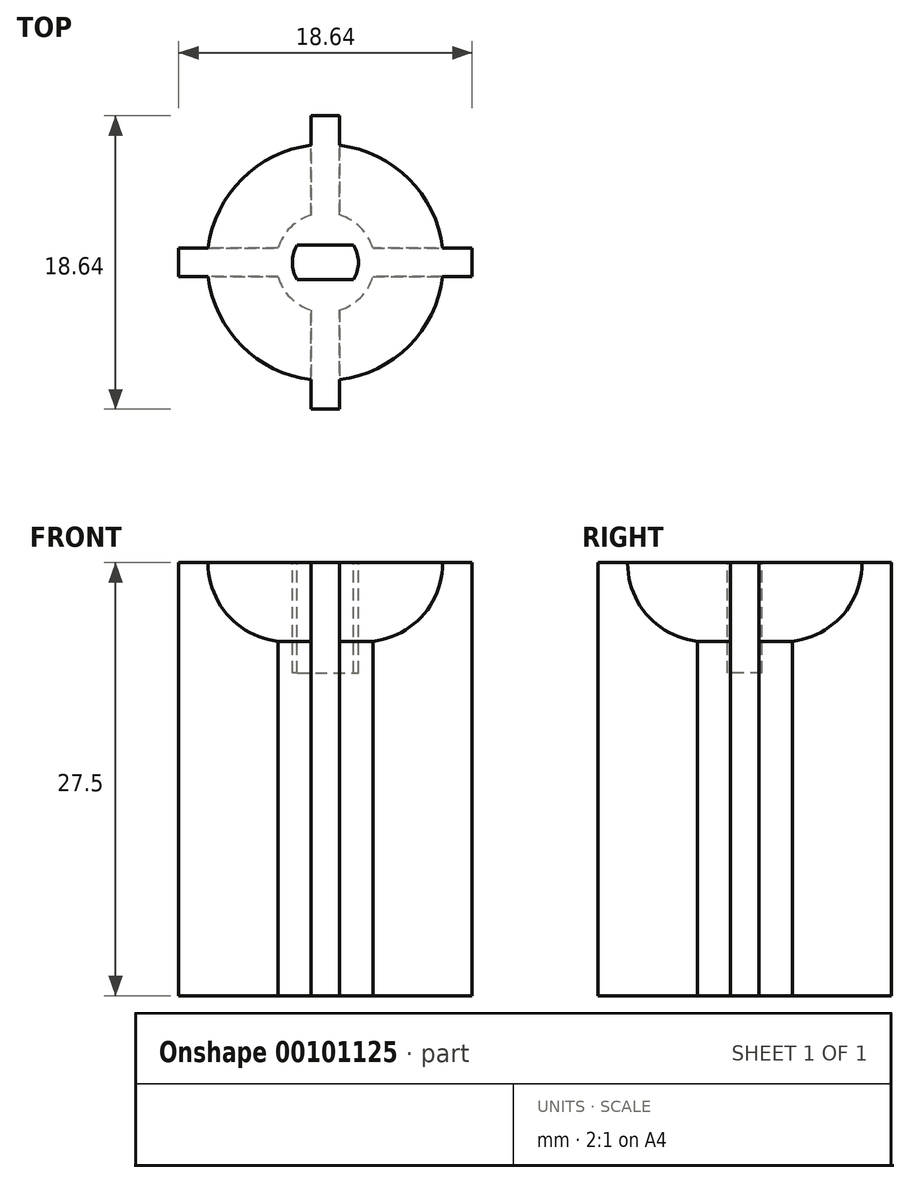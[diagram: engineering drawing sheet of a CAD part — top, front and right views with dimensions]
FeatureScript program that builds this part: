
annotation { "Feature Type Name" : "Feature", "Feature Type Description" : "" }
export const myFeature = defineFeature(function(context is Context, id is Id, definition is map)
    precondition{}
    {
        {
            var Q0;
            Q0=qCreatedBy(makeId("Top.planeOp"),FACE);
            var sketch = newSketch(context, id + "F0", { "sketchPlane" : qUnion([Q0])});
            skCircle(sketch, "E0", {"center": v(0, 0) * mm, "radius": 3.15 * mm});
            skLineSegment(sketch, "E1", {"start": v(-3.02, 0.9) * mm, "end": v(-9.32, 0.9) * mm});
            skLineSegment(sketch, "E2", {"start": v(-9.32, 0.9) * mm, "end": v(-9.32, -0.9) * mm});
            skLineSegment(sketch, "E3", {"start": v(-9.32, -0.9) * mm, "end": v(-3.02, -0.9) * mm});
            skLineSegment(sketch, "E4.1.0", {"start": v(-0.9, -3.02) * mm, "end": v(-0.9, -9.32) * mm});
            skLineSegment(sketch, "E4.1.1", {"start": v(-0.9, -9.32) * mm, "end": v(0.9, -9.32) * mm});
            skLineSegment(sketch, "E4.1.2", {"start": v(0.9, -9.32) * mm, "end": v(0.9, -3.02) * mm});
            skLineSegment(sketch, "E4.2.0", {"start": v(3.02, -0.9) * mm, "end": v(9.32, -0.9) * mm});
            skLineSegment(sketch, "E4.2.1", {"start": v(9.32, -0.9) * mm, "end": v(9.32, 0.9) * mm});
            skLineSegment(sketch, "E4.2.2", {"start": v(9.32, 0.9) * mm, "end": v(3.02, 0.9) * mm});
            skLineSegment(sketch, "E4.3.0", {"start": v(0.9, 3.02) * mm, "end": v(0.9, 9.32) * mm});
            skLineSegment(sketch, "E4.3.1", {"start": v(0.9, 9.32) * mm, "end": v(-0.9, 9.32) * mm});
            skLineSegment(sketch, "E4.3.2", {"start": v(-0.9, 9.32) * mm, "end": v(-0.9, 3.02) * mm});
            skSolve(sketch);
        }
        {
            var Q0;
            Q0 = qSketchRegion(id + "F0", true);
            extrude(context, id + "F1", {"entities" : qUnion([Q0]), "depth" : 25 * mm});
        }
        {
            var Q0;
            Q0=makeQuery(id+"F1.opExtrude","CAP_FACE",FACE,{"disambiguationData":[OSD([sQuery(id+"F0.wireOp",EDGE,"E0"),sQuery(id+"F0.wireOp",EDGE,"E1"),sQuery(id+"F0.wireOp",EDGE,"E2"),sQuery(id+"F0.wireOp",EDGE,"E3"),sQuery(id+"F0.wireOp",EDGE,"3edc4b27-075a-45ef-aea2-eed3a7496e3e2.MirrorCS"),sQuery(id+"F0.wireOp",EDGE,"3edc4b27-075a-45ef-aea2-eed3a7496e3e4.MirrorCS"),sQuery(id+"F0.wireOp",EDGE,"q4PIojLU-buq7-G7pm-UIdF-VrHVZa9xzF9O")])],"isStart":false});
            var sketch = newSketch(context, id + "F2", { "sketchPlane" : qUnion([Q0])});
            skCircle(sketch, "E5", {"center": v(0, 0) * mm, "radius": 2.1 * mm});
            skLineSegment(sketch, "E6", {"start": v(-1.79, 1.1) * mm, "end": v(1.79, 1.1) * mm});
            skLineSegment(sketch, "E7", {"start": v(-1.79, -1.1) * mm, "end": v(1.79, -1.1) * mm});
            skSolve(sketch);
        }
        {
            var Q0;
            {var subQ0=sQuery(id+"F2.wireOp",EDGE,"E6");Q0=makeQuery(id+"F2.imprint","IMPRINT",FACE,{"disambiguationData":[TD([[makeQuery(id+"F2.imprint","IMPRINT",EDGE,{"derivedFrom":subQ0}),-1.0]])]});}
            extrude(context, id + "F3", {"entities" : qUnion([Q0]), "operationType" : NewBodyOperationType.REMOVE, "oppositeDirection" : true, "depth" : 7 * mm});
        }
        {
            var Q0;
            Q0=qCreatedBy(makeId("Front.planeOp"),FACE);
            cPlane(context, id + "F4", {"entities" : qUnion([Q0]), "cplaneType" : CPlaneType.OFFSET, "offset" : 3.25 * mm, "width" : 150 * mm, "height" : 150 * mm});
        }
        {
            var Q0;
            Q0=makeQuery(id+"F1.opExtrude","CAP_FACE",FACE,{"disambiguationData":[OSD([sQuery(id+"F0.wireOp",EDGE,"E0"),sQuery(id+"F0.wireOp",EDGE,"E1"),sQuery(id+"F0.wireOp",EDGE,"E2"),sQuery(id+"F0.wireOp",EDGE,"E3"),sQuery(id+"F0.wireOp",EDGE,"E4.1.0"),sQuery(id+"F0.wireOp",EDGE,"E4.1.1"),sQuery(id+"F0.wireOp",EDGE,"E4.1.2"),sQuery(id+"F0.wireOp",EDGE,"E4.2.0"),sQuery(id+"F0.wireOp",EDGE,"E4.2.1"),sQuery(id+"F0.wireOp",EDGE,"E4.2.2"),sQuery(id+"F0.wireOp",EDGE,"E4.3.0"),sQuery(id+"F0.wireOp",EDGE,"E4.3.1"),sQuery(id+"F0.wireOp",EDGE,"E4.3.2")])],"isStart":false});
            var sketch = newSketch(context, id + "F5", { "sketchPlane" : qUnion([Q0])});
            skCircle(sketch, "E8", {"center": v(0, 0) * mm, "radius": 7.5 * mm});
            skSolve(sketch);
        }
        {
            var Q0;
            {var subQ4=sQuery(id+"F0.wireOp",EDGE,"E1");var subQ7=sQuery(id+"F0.wireOp",EDGE,"E0");var subQ8=makeQuery(id+"F1.opExtrude","CAP_EDGE",EDGE,{"disambiguationData":[OSD([subQ7]),TDD([makeQuery(id+"F0.imprint","IMPRINT",EDGE,{"disambiguationData":[TD([[makeQuery(id+"F0.imprint","INTERSECT",VERTEX,{"derivedFrom":[subQ7,subQ4]}),1.0]])],"derivedFrom":subQ7})])],"isStart":false});Q0=makeQuery(id+"F5.imprint","IMPRINT",FACE,{"disambiguationData":[TD([[makeQuery(id+"F5.imprint","IMPRINT",EDGE,{"derivedFrom":subQ8}),-1.0]])]});}
            var Q1;
            {var subQ1=sQuery(id+"F0.wireOp",EDGE,"E3");var subQ7=sQuery(id+"F0.wireOp",EDGE,"E0");var subQ8=makeQuery(id+"F1.opExtrude","CAP_EDGE",EDGE,{"disambiguationData":[OSD([subQ7]),TDD([makeQuery(id+"F0.imprint","IMPRINT",EDGE,{"disambiguationData":[TD([[makeQuery(id+"F0.imprint","INTERSECT",VERTEX,{"derivedFrom":[subQ7,subQ1]}),-1.0]])],"derivedFrom":subQ7})])],"isStart":false});Q1=makeQuery(id+"F5.imprint","IMPRINT",FACE,{"disambiguationData":[TD([[makeQuery(id+"F5.imprint","IMPRINT",EDGE,{"derivedFrom":subQ8}),-1.0]])]});}
            var Q2;
            {var subQ1=sQuery(id+"F0.wireOp",EDGE,"E4.1.2");var subQ7=sQuery(id+"F0.wireOp",EDGE,"E0");var subQ8=makeQuery(id+"F1.opExtrude","CAP_EDGE",EDGE,{"disambiguationData":[OSD([subQ7]),TDD([makeQuery(id+"F0.imprint","IMPRINT",EDGE,{"disambiguationData":[TD([[makeQuery(id+"F0.imprint","INTERSECT",VERTEX,{"derivedFrom":[subQ7,subQ1]}),-1.0]])],"derivedFrom":subQ7})])],"isStart":false});Q2=makeQuery(id+"F5.imprint","IMPRINT",FACE,{"disambiguationData":[TD([[makeQuery(id+"F5.imprint","IMPRINT",EDGE,{"derivedFrom":subQ8}),-1.0]])]});}
            var Q3;
            {var subQ4=sQuery(id+"F0.wireOp",EDGE,"E4.2.2");var subQ7=sQuery(id+"F0.wireOp",EDGE,"E0");var subQ8=makeQuery(id+"F1.opExtrude","CAP_EDGE",EDGE,{"disambiguationData":[OSD([subQ7]),TDD([makeQuery(id+"F0.imprint","IMPRINT",EDGE,{"disambiguationData":[TD([[makeQuery(id+"F0.imprint","INTERSECT",VERTEX,{"derivedFrom":[subQ7,subQ4]}),-1.0]])],"derivedFrom":subQ7})])],"isStart":false});Q3=makeQuery(id+"F5.imprint","IMPRINT",FACE,{"disambiguationData":[TD([[makeQuery(id+"F5.imprint","IMPRINT",EDGE,{"derivedFrom":subQ8}),-1.0]])]});}
            extrude(context, id + "F6", {"entities" : qUnion([Q0, Q1, Q2, Q3]), "operationType" : NewBodyOperationType.ADD, "oppositeDirection" : true, "depth" : 5 * mm});
        }
        {
            var Q0;
            Q0=makeQuery(id+"F1.opExtrude","CAP_FACE",FACE,{"disambiguationData":[OSD([sQuery(id+"F0.wireOp",EDGE,"E0"),sQuery(id+"F0.wireOp",EDGE,"E1"),sQuery(id+"F0.wireOp",EDGE,"E2"),sQuery(id+"F0.wireOp",EDGE,"E3"),sQuery(id+"F0.wireOp",EDGE,"E4.1.0"),sQuery(id+"F0.wireOp",EDGE,"E4.1.1"),sQuery(id+"F0.wireOp",EDGE,"E4.1.2"),sQuery(id+"F0.wireOp",EDGE,"E4.2.0"),sQuery(id+"F0.wireOp",EDGE,"E4.2.1"),sQuery(id+"F0.wireOp",EDGE,"E4.2.2"),sQuery(id+"F0.wireOp",EDGE,"E4.3.0"),sQuery(id+"F0.wireOp",EDGE,"E4.3.1"),sQuery(id+"F0.wireOp",EDGE,"E4.3.2")])],"isStart":true});
            extrude(context, id + "F7", {"entities" : qUnion([Q0]), "operationType" : NewBodyOperationType.ADD, "depth" : 2.5 * mm});
        }
        {
            var Q0;
            {var subQ0=sQuery(id+"F5.wireOp",EDGE,"E8");Q0=makeQuery(id+"F6.opExtrude","CAP_EDGE",EDGE,{"disambiguationData":[OSD([subQ0]),TDD([makeQuery(id+"F5.imprint","IMPRINT",EDGE,{"disambiguationData":[TD([[makeQuery(id+"F5.imprint","INTERSECT",VERTEX,{"derivedFrom":[makeQuery(id+"F1.opExtrude","CAP_EDGE",EDGE,{"disambiguationData":[OSD([sQuery(id+"F0.wireOp",EDGE,"E4.3.2")])],"isStart":false}),subQ0]}),-1.0]])],"derivedFrom":subQ0})])],"isStart":false});}
            var Q1;
            {var subQ0=sQuery(id+"F5.wireOp",EDGE,"E8");Q1=makeQuery(id+"F6.opExtrude","CAP_EDGE",EDGE,{"disambiguationData":[OSD([subQ0]),TDD([makeQuery(id+"F5.imprint","IMPRINT",EDGE,{"disambiguationData":[TD([[makeQuery(id+"F5.imprint","INTERSECT",VERTEX,{"derivedFrom":[makeQuery(id+"F1.opExtrude","CAP_EDGE",EDGE,{"disambiguationData":[OSD([sQuery(id+"F0.wireOp",EDGE,"E4.3.0")])],"isStart":false}),subQ0]}),1.0]])],"derivedFrom":subQ0})])],"isStart":false});}
            var Q2;
            {var subQ0=sQuery(id+"F5.wireOp",EDGE,"E8");Q2=makeQuery(id+"F6.opExtrude","CAP_EDGE",EDGE,{"disambiguationData":[OSD([subQ0]),TDD([makeQuery(id+"F5.imprint","IMPRINT",EDGE,{"disambiguationData":[TD([[makeQuery(id+"F5.imprint","INTERSECT",VERTEX,{"derivedFrom":[makeQuery(id+"F1.opExtrude","CAP_EDGE",EDGE,{"disambiguationData":[OSD([sQuery(id+"F0.wireOp",EDGE,"E3")])],"isStart":false}),subQ0]}),-1.0]])],"derivedFrom":subQ0})])],"isStart":false});}
            var Q3;
            {var subQ0=sQuery(id+"F5.wireOp",EDGE,"E8");Q3=makeQuery(id+"F6.opExtrude","CAP_EDGE",EDGE,{"disambiguationData":[OSD([subQ0]),TDD([makeQuery(id+"F5.imprint","IMPRINT",EDGE,{"disambiguationData":[TD([[makeQuery(id+"F5.imprint","INTERSECT",VERTEX,{"derivedFrom":[makeQuery(id+"F1.opExtrude","CAP_EDGE",EDGE,{"disambiguationData":[OSD([sQuery(id+"F0.wireOp",EDGE,"E4.1.2")])],"isStart":false}),subQ0]}),-1.0]])],"derivedFrom":subQ0})])],"isStart":false});}
            fillet(context, id + "F8", {"entities" : qUnion([Q0, Q1, Q2, Q3]), "radius" : 5 * mm, "tangentPropagation" : true, "allowEdgeOverflow" : false});
        }
    });
